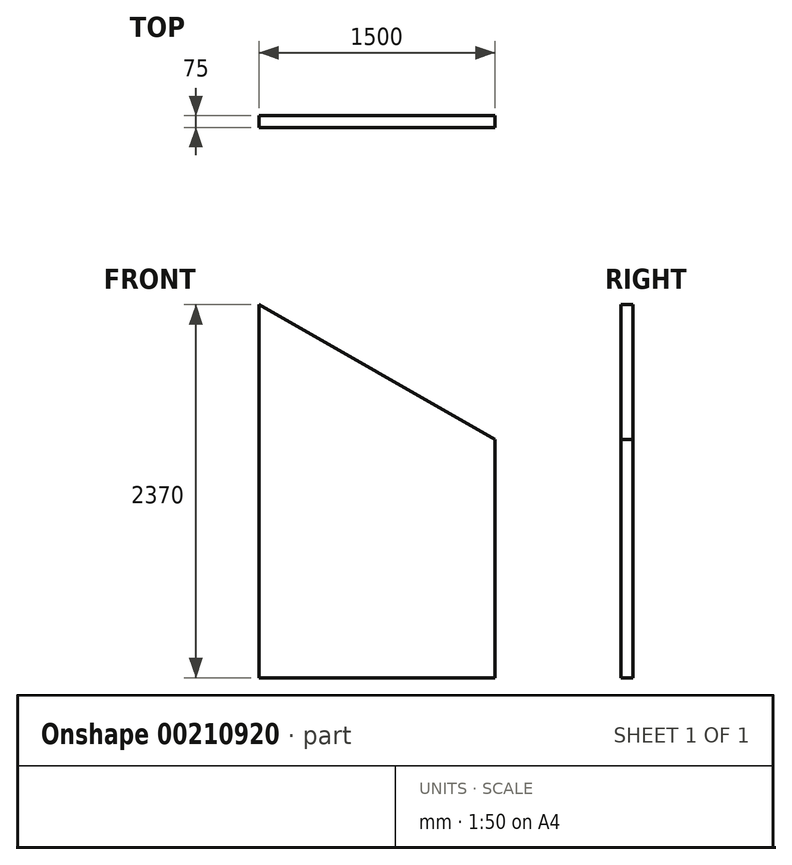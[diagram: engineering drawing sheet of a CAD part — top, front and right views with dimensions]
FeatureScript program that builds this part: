
annotation { "Feature Type Name" : "Feature", "Feature Type Description" : "" }
export const myFeature = defineFeature(function(context is Context, id is Id, definition is map)
    precondition{}
    {
        {
            var Q0;
            Q0=qCreatedBy(makeId("Front.planeOp"),FACE);
            var sketch = newSketch(context, id + "F0", { "sketchPlane" : qUnion([Q0])});
            skLineSegment(sketch, "E0.bottom", {"start": v(0, 0) * mm, "end": v(1500, 0) * mm});
            skLineSegment(sketch, "E0.right", {"start": v(1500, 0) * mm, "end": v(1500, 1514) * mm});
            skLineSegment(sketch, "E1", {"start": v(0, 2370) * mm, "end": v(1500, 1514) * mm});
            skLineSegment(sketch, "E2", {"start": v(0, 0) * mm, "end": v(0, 2370) * mm});
            skSolve(sketch);
        }
        {
            var Q0;
            Q0=makeQuery(id+"F0.imprint","IMPRINT",FACE,{"disambiguationData":[TD([[makeQuery(id+"F0.imprint","IMPRINT",EDGE,{"derivedFrom":sQuery(id+"F0.wireOp",EDGE,"E0.bottom")}),1.0]])]});
            extrude(context, id + "F1", {"entities" : qUnion([Q0]), "depth" : 75 * mm});
        }
    });
